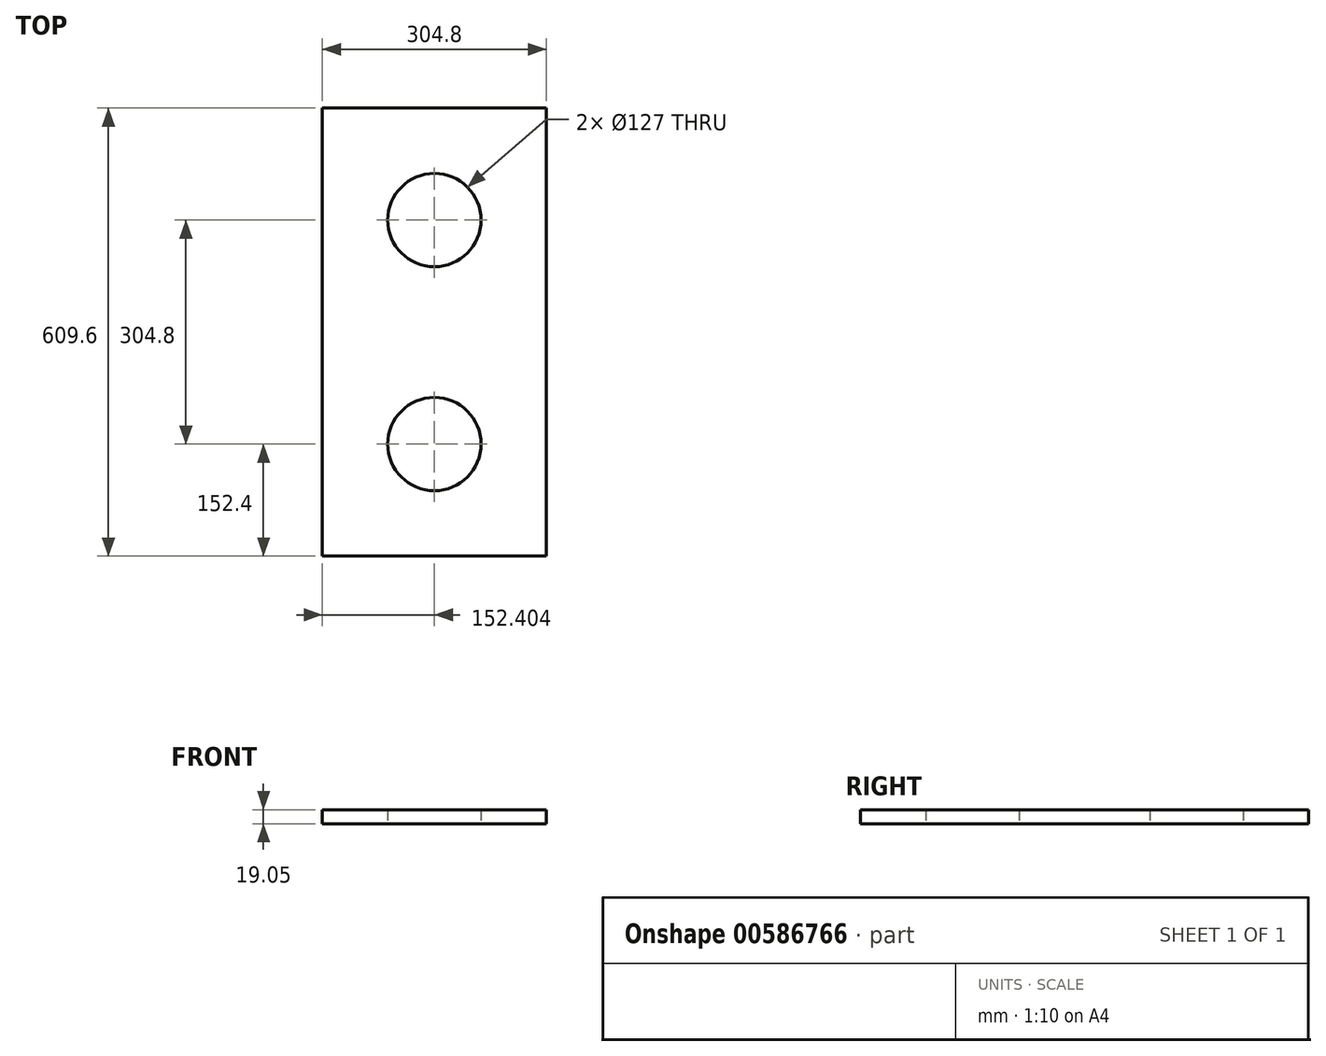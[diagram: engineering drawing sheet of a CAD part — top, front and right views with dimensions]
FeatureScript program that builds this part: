
annotation { "Feature Type Name" : "Feature", "Feature Type Description" : "" }
export const myFeature = defineFeature(function(context is Context, id is Id, definition is map)
    precondition{}
    {
        {
            var Q0;
            Q0=qCreatedBy(makeId("Top.planeOp"),FACE);
            var sketch = newSketch(context, id + "F0", { "sketchPlane" : qUnion([Q0])});
            skLineSegment(sketch, "E0.bottom", {"start": v(-480.7, 310.58) * mm, "end": v(-175.9, 310.58) * mm});
            skLineSegment(sketch, "E0.top", {"start": v(-480.7, -299.02) * mm, "end": v(-175.9, -299.02) * mm});
            skLineSegment(sketch, "E0.left", {"start": v(-480.7, 310.58) * mm, "end": v(-480.7, -299.02) * mm});
            skLineSegment(sketch, "E0.right", {"start": v(-175.9, 310.58) * mm, "end": v(-175.9, -299.02) * mm});
            skCircle(sketch, "E1", {"center": v(-328.3, 158.18) * mm, "radius": 63.5 * mm});
            skCircle(sketch, "E2", {"center": v(-328.3, -146.62) * mm, "radius": 63.5 * mm});
            skSolve(sketch);
        }
        {
            var Q0;
            Q0=makeQuery(id+"F0.imprint","IMPRINT",FACE,{"disambiguationData":[TD([[makeQuery(id+"F0.imprint","IMPRINT",EDGE,{"derivedFrom":sQuery(id+"F0.wireOp",EDGE,"E0.bottom")}),-1.0]])]});
            extrude(context, id + "F1", {"entities" : qUnion([Q0]), "depth" : 19.05 * mm, "offsetDistance" : 25.4 * mm});
        }
    });
